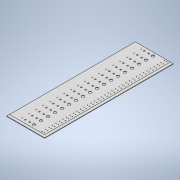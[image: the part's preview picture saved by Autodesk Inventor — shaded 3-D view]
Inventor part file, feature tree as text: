
AUTODESK INVENTOR PART (.ipt)
format: ipt  version: 2021.2 (Build 252289000, 289)  size: 295,424 bytes
history: native  units: in
note: dims shown in document units (in); Inventor stores cm internally (conversion verified against a paired STEP export)
features: extrude x6, sketch x6, pattern_linear x2
ambient origin geometry x8: Origin, YZ Plane, XZ Plane, XY Plane, X Axis, Y Axis, Z Axis, Center Point
bodies: Solid1 (feature_tree)
feature tree (14):
  extrude  "Extrusion1"  Depth=0.0312in
  extrude  "Extrusion2"  Depth=0.25in
  pattern_linear  "Rectangular Pattern1"  Spacing1=1.7in  [1 undecoded]
  extrude  "Extrusion3"  Depth=0.0156in
  pattern_linear  "Rectangular Pattern2"  Spacing1=0.3in  [1 undecoded]
  extrude  "Extrusion4"  Depth=0.0156in
  extrude  "Extrusion5"  Depth=0.0156in
  extrude  "Extrusion6"  Depth=0.0156in
  sketch  "Sketch1"  dims[d0=3.25in d1=0.0312in]
  sketch  "Sketch2"  dims[d2=11.625in d3=0.0in d8=0.25in]
  sketch  "Sketch3"  dims[d9=0.125in]
  sketch  "Sketch4"  dims[d10=0.125in]
  sketch  "Sketch5"  dims[d11=0.0625in]
  sketch  "Sketch6"  dims[d12=1.3in d13=1.7in d14=2.1in d16=0.3in d19=0.3229in d20=0.3229in d21=0.3229in d22=0.3229in d23=0.0in d24=0.0in d25=7.0866in d27=0.6458in d28=0.0625in d29=0.0625in d30=0.2in d31=0.4in d32=0.1615in d33=0.1615in d34=0.0in d35=0.0in d36=14.1732in d38=0.3229in d39=0.25in d40=0.0in d41=0.25in d42=0.0in d43=0.25in d44=0.25in d45=0.0156in d46=0.0in]
note: 2 required parameter values undecoded (feature->parameter linkage not recoverable at this tier; creation-order binding heuristic only, values carry confidence <= 0.55)
